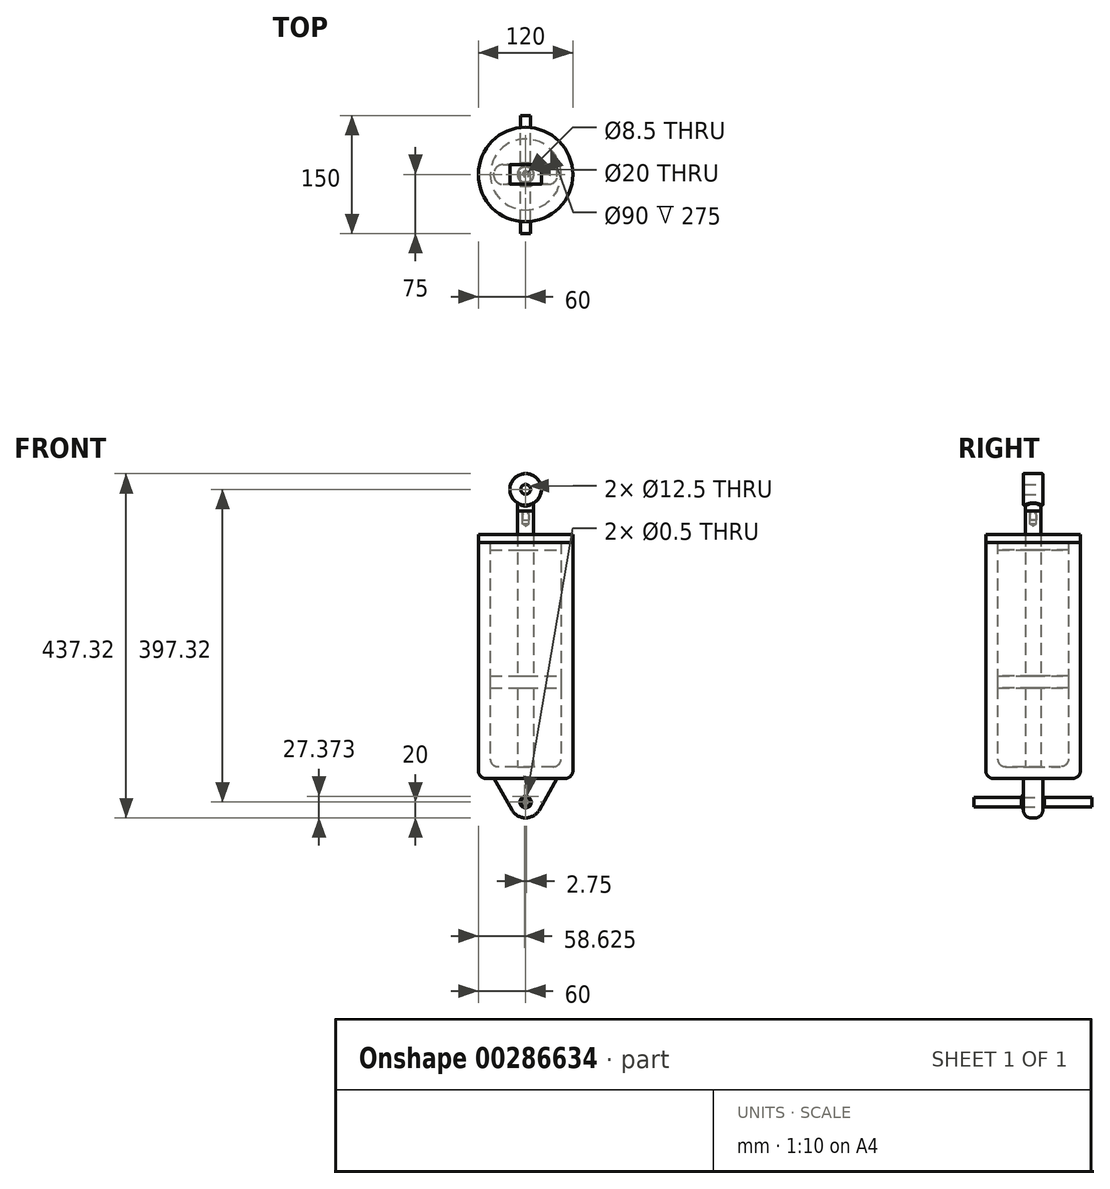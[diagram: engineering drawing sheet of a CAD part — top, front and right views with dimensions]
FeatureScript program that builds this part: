
annotation { "Feature Type Name" : "Feature", "Feature Type Description" : "" }
export const myFeature = defineFeature(function(context is Context, id is Id, definition is map)
    precondition{}
    {
        {
            var Q0;
            Q0=qCreatedBy(makeId("Top.planeOp"),FACE);
            var sketch = newSketch(context, id + "F0", { "sketchPlane" : qUnion([Q0])});
            skCircle(sketch, "E0", {"center": v(0, 0) * mm, "radius": 60 * mm});
            skSolve(sketch);
        }
        {
            var Q0;
            Q0 = qSketchRegion(id + "F0", true);
            extrude(context, id + "F1", {"entities" : qUnion([Q0]), "depth" : 300 * mm});
        }
        {
            var Q0;
            Q0=makeQuery(id+"F1.opExtrude","CAP_FACE",FACE,{"disambiguationData":[OSD([sQuery(id+"F0.wireOp",EDGE,"E0")])],"isStart":false});
            shell(context, id + "F2", {"entities" : qUnion([Q0]), "thickness" : 15 * mm});
        }
        {
            var Q0;
            Q0=qCreatedBy(makeId("Front.planeOp"),FACE);
            var sketch = newSketch(context, id + "F3", { "sketchPlane" : qUnion([Q0])});
            skLineSegment(sketch, "E1", {"start": v(40, 0) * mm, "end": v(17.4, -39.86) * mm});
            skLineSegment(sketch, "E2", {"start": v(-17.4, -39.86) * mm, "end": v(-40, 0) * mm});
            skLineSegment(sketch, "E3", {"start": v(-40, 0) * mm, "end": v(40, 0) * mm});
            skPoint(sketch, "E4.visualSharp", {"position": v(0, -70.55) * mm});
            skArc(sketch, "E4.filletArc", {"start": v(-17.4, -39.86) * mm, "mid": v(0, -50) * mm, "end": v(17.4, -39.86) * mm});
            skLineSegment(sketch, "E5", {"start": v(0, 0) * mm, "end": v(0, -40.4) * mm, "construction": true});
            skCircle(sketch, "E6", {"center": v(0, -30) * mm, "radius": 6.25 * mm});
            skSolve(sketch);
        }
        {
            var Q0;
            Q0 = qSketchRegion(id + "F3", true);
            extrude(context, id + "F4", {"entities" : qUnion([Q0]), "operationType" : NewBodyOperationType.ADD, "endBound" : BoundingType.SYMMETRIC, "depth" : 25 * mm});
        }
        {
            var Q0;
            Q0=makeQuery(id+"F1.opExtrude","CAP_EDGE",EDGE,{"disambiguationData":[OSD([sQuery(id+"F0.wireOp",EDGE,"E0")])],"isStart":true});
            var Q1;
            Q1=makeQuery(id+"F4.opExtrude","CAP_EDGE",EDGE,{"disambiguationData":[OSD([sQuery(id+"F3.wireOp",EDGE,"E3")])],"isStart":true});
            var Q2;
            Q2=makeQuery(id+"F4.opExtrude","CAP_EDGE",EDGE,{"disambiguationData":[OSD([sQuery(id+"F3.wireOp",EDGE,"E3")])],"isStart":false});
            var Q3;
            Q3=makeQuery(id+"F4.opExtrude","CAP_EDGE",EDGE,{"disambiguationData":[OSD([sQuery(id+"F3.wireOp",EDGE,"E2")])],"isStart":false});
            var Q4;
            Q4=makeQuery(id+"F4.opExtrude","CAP_EDGE",EDGE,{"disambiguationData":[OSD([sQuery(id+"F3.wireOp",EDGE,"E2")])],"isStart":true});
            fillet(context, id + "F5", {"entities" : qUnion([Q0, Q1, Q2, Q3, Q4]), "radius" : 10 * mm, "tangentPropagation" : true, "allowEdgeOverflow" : false});
        }
        {
            var Q0;
            {var subQ0=sQuery(id+"F0.wireOp",EDGE,"E0");Q0=makeQuery(id+"F2.opShell","OFFSET_EDGE",EDGE,{"disambiguationData":[OSD([subQ0]),TDD([makeQuery(id+"F1.opExtrude","CAP_EDGE",EDGE,{"disambiguationData":[OSD([subQ0])],"isStart":true})])]});}
            fillet(context, id + "F6", {"entities" : qUnion([Q0]), "radius" : 10 * mm, "tangentPropagation" : true, "allowEdgeOverflow" : false});
        }
        {
            var Q0;
            Q0=qCreatedBy(makeId("Front.planeOp"),FACE);
            var sketch = newSketch(context, id + "F7", { "sketchPlane" : qUnion([Q0])});
            skLineSegment(sketch, "E7", {"start": v(45, 300) * mm, "end": v(45, 290) * mm});
            skLineSegment(sketch, "E8", {"start": v(0, 310) * mm, "end": v(60, 310) * mm});
            skLineSegment(sketch, "E9", {"start": v(60, 310) * mm, "end": v(60, 300) * mm});
            skLineSegment(sketch, "E10", {"start": v(0, 290) * mm, "end": v(45, 290) * mm});
            skLineSegment(sketch, "E11.trimOffspring", {"start": v(45, 300) * mm, "end": v(60, 300) * mm});
            skLineSegment(sketch, "E12", {"start": v(0, 290) * mm, "end": v(0, 310) * mm});
            skPoint(sketch, "E13.end.orphan", {"position": v(-60, 310) * mm});
            skPoint(sketch, "E14.0.start.orphan", {"position": v(-60, 300) * mm});
            skLineSegment(sketch, "E15", {"start": v(0, 0) * mm, "end": v(0, 290) * mm, "construction": true});
            skSolve(sketch);
        }
        {
            var Q0;
            Q0 = qSketchRegion(id + "F7", true);
            var Q1;
            Q1=sQuery(id+"F7.wireOp",EDGE,"E12");
            revolve(context, id + "F8", {"entities" : qUnion([Q0]), "axis" : qUnion([Q1]), "revolveType" : RevolveType.FULL});
        }
        {
            var Q0;
            Q0=qCreatedBy(makeId("Front.planeOp"),FACE);
            var sketch = newSketch(context, id + "F9", { "sketchPlane" : qUnion([Q0])});
            skLineSegment(sketch, "E16", {"start": v(0, 15) * mm, "end": v(0, 340) * mm});
            skLineSegment(sketch, "E17", {"start": v(0, 340) * mm, "end": v(10, 340) * mm});
            skLineSegment(sketch, "E18", {"start": v(10, 340) * mm, "end": v(10, 130) * mm});
            skLineSegment(sketch, "E19", {"start": v(10, 130) * mm, "end": v(45, 130) * mm});
            skLineSegment(sketch, "E20", {"start": v(45, 115) * mm, "end": v(10, 115) * mm});
            skLineSegment(sketch, "E21", {"start": v(10, 115) * mm, "end": v(10, 15) * mm});
            skLineSegment(sketch, "E22", {"start": v(10, 15) * mm, "end": v(0, 15) * mm});
            skLineSegment(sketch, "E23", {"start": v(45, 130) * mm, "end": v(45, 115) * mm});
            skSolve(sketch);
        }
        {
            var Q0;
            Q0 = qSketchRegion(id + "F9", true);
            var Q1;
            Q1=sQuery(id+"F9.wireOp",EDGE,"E16");
            revolve(context, id + "F10", {"entities" : qUnion([Q0]), "axis" : qUnion([Q1]), "revolveType" : RevolveType.FULL});
        }
        {
            var Q0;
            Q0=makeQuery(id+"F10.opRevolve","SWEPT_BODY",BODY,{"disambiguationData":[OSD([sQuery(id+"F9.wireOp",EDGE,"E16"),sQuery(id+"F9.wireOp",EDGE,"E17"),sQuery(id+"F9.wireOp",EDGE,"E18"),sQuery(id+"F9.wireOp",EDGE,"E19"),sQuery(id+"F9.wireOp",EDGE,"E20"),sQuery(id+"F9.wireOp",EDGE,"E21"),sQuery(id+"F9.wireOp",EDGE,"E22"),sQuery(id+"F9.wireOp",EDGE,"E23")])]});
            var Q1;
            Q1=makeQuery(id+"F8.opRevolve","SWEPT_BODY",BODY,{"disambiguationData":[OSD([sQuery(id+"F7.wireOp",EDGE,"E7"),sQuery(id+"F7.wireOp",EDGE,"E8"),sQuery(id+"F7.wireOp",EDGE,"E9"),sQuery(id+"F7.wireOp",EDGE,"E10"),sQuery(id+"F7.wireOp",EDGE,"E11.trimOffspring"),sQuery(id+"F7.wireOp",EDGE,"E12")])]});
            booleanBodies(context, id + "F11", {"operationType" : BooleanOperationType.SUBTRACTION, "tools" : qUnion([Q0]), "targets" : qUnion([Q1]), "keepTools" : true});
        }
        {
            var Q0;
            Q0=makeQuery(id+"F10.opRevolve","SWEPT_FACE",FACE,{"disambiguationData":[OSD([sQuery(id+"F9.wireOp",EDGE,"E17")])]});
            var sketch = newSketch(context, id + "F12", { "sketchPlane" : qUnion([Q0])});
            skPoint(sketch, "E24", {"position": v(0, 0) * mm});
            skSolve(sketch);
        }
        {
            var Q0;
            Q0=sQuery(id+"F12.wireOp",VERTEX,"E24");
            var Q1;
            Q1=makeQuery(id+"F10.opRevolve","SWEPT_BODY",BODY,{"disambiguationData":[OSD([sQuery(id+"F9.wireOp",EDGE,"E16"),sQuery(id+"F9.wireOp",EDGE,"E17"),sQuery(id+"F9.wireOp",EDGE,"E18"),sQuery(id+"F9.wireOp",EDGE,"E19"),sQuery(id+"F9.wireOp",EDGE,"E20"),sQuery(id+"F9.wireOp",EDGE,"E21"),sQuery(id+"F9.wireOp",EDGE,"E22"),sQuery(id+"F9.wireOp",EDGE,"E23")])]});
            hole(context, id + "F13", {"style" : HoleStyle.SIMPLE, "endStyle" : HoleEndStyle.BLIND, "standardTappedOrClearance" : lookupTablePath({ "standard" : "ISO", "fit" : "Normal", "engagement" : "75%", "pitch" : "1.5 mm", "size" : "M10", "type" : "Tapped" }), "standardBlindInLast" : lookupTablePath({ "fit" : "Standard", "standard" : "ISO", "engagement" : "75%", "pitch" : "1.5 mm", "size" : "M10", "type" : "Tapped" }), "holeDiameter" : 8.5 * mm, "showTappedDepth" : true, "holeDepth" : 16.5 * mm, "tappedDepth" : 12 * mm, "tapClearance" : 3, "locations" : qUnion([Q0]), "scope" : qUnion([Q1]), "majorDiameter" : 10 * mm});
        }
        {
            var Q0;
            Q0=qCreatedBy(makeId("Front.planeOp"),FACE);
            var sketch = newSketch(context, id + "F14", { "sketchPlane" : qUnion([Q0])});
            skLineSegment(sketch, "E25", {"start": v(4.25, 334) * mm, "end": v(4.25, 328.5) * mm});
            skLineSegment(sketch, "E26", {"start": v(0, 328.5) * mm, "end": v(4.25, 328.5) * mm});
            skLineSegment(sketch, "E27.0", {"start": v(10, 340) * mm, "end": v(5.14, 340) * mm});
            skLineSegment(sketch, "E28", {"start": v(0, 328.5) * mm, "end": v(0, 350) * mm});
            skLineSegment(sketch, "E29", {"start": v(0, 350) * mm, "end": v(10, 350) * mm});
            skLineSegment(sketch, "E30", {"start": v(10, 350) * mm, "end": v(10, 340) * mm});
            skPoint(sketch, "E31.start.orphan", {"position": v(-4.25, 328.5) * mm});
            skPoint(sketch, "E32.orphan", {"position": v(-10, 340) * mm});
            skPoint(sketch, "E33", {"position": v(0, 340) * mm});
            skLineSegment(sketch, "E34", {"start": v(3.14, 338) * mm, "end": v(3.14, 337) * mm});
            skLineSegment(sketch, "E35", {"start": v(3.4, 336) * mm, "end": v(3.98, 335) * mm});
            skPoint(sketch, "E36.visualSharp", {"position": v(3.14, 338.83) * mm});
            skArc(sketch, "E36.filletArc", {"start": v(5.14, 340) * mm, "mid": v(3.72, 339.41) * mm, "end": v(3.14, 338) * mm});
            skPoint(sketch, "E37.visualSharp", {"position": v(4.25, 334.54) * mm});
            skArc(sketch, "E37.filletArc", {"start": v(4.25, 334) * mm, "mid": v(4.18, 334.52) * mm, "end": v(3.98, 335) * mm});
            skPoint(sketch, "E38.visualSharp", {"position": v(3.14, 336.46) * mm});
            skArc(sketch, "E38.filletArc", {"start": v(3.14, 337) * mm, "mid": v(3.2, 336.48) * mm, "end": v(3.4, 336) * mm});
            skSolve(sketch);
        }
        {
            var Q0;
            Q0 = qSketchRegion(id + "F14", true);
            var Q1;
            Q1=sQuery(id+"F14.wireOp",EDGE,"E28");
            revolve(context, id + "F15", {"entities" : qUnion([Q0]), "axis" : qUnion([Q1]), "revolveType" : RevolveType.FULL});
        }
        {
            var Q0;
            Q0=qCreatedBy(makeId("Front.planeOp"),FACE);
            var sketch = newSketch(context, id + "F16", { "sketchPlane" : qUnion([Q0])});
            skCircle(sketch, "E39", {"center": v(0, 367.32) * mm, "radius": 20 * mm});
            skCircle(sketch, "E40", {"center": v(0, 367.32) * mm, "radius": 6.25 * mm});
            skSolve(sketch);
        }
        {
            var Q0;
            Q0 = qSketchRegion(id + "F16", true);
            extrude(context, id + "F17", {"entities" : qUnion([Q0]), "operationType" : NewBodyOperationType.ADD, "endBound" : BoundingType.SYMMETRIC, "depth" : 25 * mm});
        }
        {
            var Q0;
            Q0=makeQuery(id+"F17.opExtrude","CAP_EDGE",EDGE,{"disambiguationData":[OSD([sQuery(id+"F16.wireOp",EDGE,"E39")])],"isStart":false});
            var Q1;
            Q1=makeQuery(id+"F17.opExtrude","CAP_EDGE",EDGE,{"disambiguationData":[OSD([sQuery(id+"F16.wireOp",EDGE,"E39")])],"isStart":true});
            var Q2;
            Q2=makeQuery(id+"F17.boolean.opBoolean","INTERSECT",EDGE,{"derivedFrom":[makeQuery(id+"F15.opRevolve","SWEPT_FACE",FACE,{"disambiguationData":[OSD([sQuery(id+"F14.wireOp",EDGE,"E30")])]}),makeQuery(id+"F17.opExtrude","SWEPT_FACE",FACE,{"disambiguationData":[OSD([sQuery(id+"F16.wireOp",EDGE,"E39")])]})]});
            var Q3;
            Q3=makeQuery(id+"F17.opExtrude","CAP_EDGE",EDGE,{"disambiguationData":[OSD([sQuery(id+"F16.wireOp",EDGE,"E40")])],"isStart":false});
            var Q4;
            Q4=makeQuery(id+"F17.opExtrude","CAP_EDGE",EDGE,{"disambiguationData":[OSD([sQuery(id+"F16.wireOp",EDGE,"E40")])],"isStart":true});
            fillet(context, id + "F18", {"entities" : qUnion([Q0, Q1, Q2, Q3, Q4]), "radius" : 1 * mm, "tangentPropagation" : true, "allowEdgeOverflow" : false});
        }
        {
            var Q0;
            Q0=qCreatedBy(makeId("Right.planeOp"),FACE);
            var sketch = newSketch(context, id + "F19", { "sketchPlane" : qUnion([Q0])});
            skLineSegment(sketch, "E41", {"start": v(12.5, -36.25) * mm, "end": v(-12.5, -36.25) * mm});
            skLineSegment(sketch, "E42", {"start": v(-12.5, -23.75) * mm, "end": v(12.5, -23.75) * mm, "construction": true});
            skLineSegment(sketch, "E43", {"start": v(12.5, -30) * mm, "end": v(-12.5, -30) * mm, "construction": true});
            skLineSegment(sketch, "E44", {"start": v(12.5, -36.25) * mm, "end": v(12.5, -34.25) * mm});
            skLineSegment(sketch, "E45", {"start": v(12.5, -34.25) * mm, "end": v(14.5, -34.25) * mm});
            skLineSegment(sketch, "E46", {"start": v(14.5, -34.25) * mm, "end": v(14.5, -36.25) * mm});
            skLineSegment(sketch, "E47", {"start": v(14.5, -36.25) * mm, "end": v(75, -36.25) * mm});
            skLineSegment(sketch, "E48", {"start": v(75, -36.25) * mm, "end": v(75, -30) * mm});
            skLineSegment(sketch, "E49", {"start": v(75, -30) * mm, "end": v(-75, -30) * mm});
            skLineSegment(sketch, "E50", {"start": v(-75, -30) * mm, "end": v(-75, -36.25) * mm});
            skLineSegment(sketch, "E51", {"start": v(-75, -36.25) * mm, "end": v(-14.5, -36.25) * mm});
            skLineSegment(sketch, "E52", {"start": v(-14.5, -36.25) * mm, "end": v(-14.5, -34.25) * mm});
            skLineSegment(sketch, "E53", {"start": v(-14.5, -34.25) * mm, "end": v(-12.5, -34.25) * mm});
            skLineSegment(sketch, "E54", {"start": v(-12.5, -34.25) * mm, "end": v(-12.5, -36.25) * mm});
            skLineSegment(sketch, "E55", {"start": v(0, 0) * mm, "end": v(0, -56.18) * mm, "construction": true});
            skSolve(sketch);
        }
        {
            var Q0;
            Q0 = qSketchRegion(id + "F19", true);
            var Q1;
            Q1=sQuery(id+"F19.wireOp",EDGE,"E49");
            revolve(context, id + "F20", {"entities" : qUnion([Q0]), "axis" : qUnion([Q1]), "revolveType" : RevolveType.FULL});
        }
        {
            var Q0;
            Q0=makeQuery(id+"F4.opExtrude","CAP_FACE",FACE,{"disambiguationData":[OSD([sQuery(id+"F3.wireOp",EDGE,"E1"),sQuery(id+"F3.wireOp",EDGE,"E2"),sQuery(id+"F3.wireOp",EDGE,"E3"),sQuery(id+"F3.wireOp",EDGE,"E4.filletArc"),sQuery(id+"F3.wireOp",EDGE,"E6")])],"isStart":false});
            var sketch = newSketch(context, id + "F21", { "sketchPlane" : qUnion([Q0])});
            skArc(sketch, "E56", {"start": v(-2.34, -23.14) * mm, "mid": v(0, -37.25) * mm, "end": v(2.34, -23.14) * mm});
            skLineSegment(sketch, "E57", {"start": v(-60, 10) * mm, "end": v(-60, 300) * mm});
            skLineSegment(sketch, "E58", {"start": v(60, 300) * mm, "end": v(60, 10) * mm});
            skArc(sketch, "E59.0", {"start": v(-1.42, -26) * mm, "mid": v(0, -34.25) * mm, "end": v(1.42, -26) * mm});
            skLineSegment(sketch, "E60", {"start": v(-0.75, -25.05) * mm, "end": v(-0.75, -22.79) * mm});
            skLineSegment(sketch, "E61", {"start": v(0.75, -25.05) * mm, "end": v(0.75, -22.79) * mm});
            skLineSegment(sketch, "E62", {"start": v(-0.75, -22.79) * mm, "end": v(-0.75, -22.2) * mm});
            skLineSegment(sketch, "E63", {"start": v(-0.95, -22) * mm, "end": v(-1.8, -22) * mm});
            skLineSegment(sketch, "E64", {"start": v(-2, -22.2) * mm, "end": v(-2, -22.66) * mm});
            skLineSegment(sketch, "E65", {"start": v(0.75, -22.79) * mm, "end": v(0.75, -22.2) * mm});
            skLineSegment(sketch, "E66", {"start": v(0.95, -22) * mm, "end": v(1.8, -22) * mm});
            skLineSegment(sketch, "E67", {"start": v(2, -22.2) * mm, "end": v(2, -22.66) * mm});
            skPoint(sketch, "E68.visualSharp", {"position": v(-0.75, -25.82) * mm});
            skArc(sketch, "E68.filletArc", {"start": v(-1.42, -26) * mm, "mid": v(-0.93, -25.63) * mm, "end": v(-0.75, -25.05) * mm});
            skPoint(sketch, "E69.visualSharp", {"position": v(0.75, -25.82) * mm});
            skArc(sketch, "E69.filletArc", {"start": v(0.75, -25.05) * mm, "mid": v(0.93, -25.63) * mm, "end": v(1.42, -26) * mm});
            skPoint(sketch, "E70.visualSharp", {"position": v(-2, -23.03) * mm});
            skArc(sketch, "E70.filletArc", {"start": v(-2.34, -23.14) * mm, "mid": v(-2.1, -22.96) * mm, "end": v(-2, -22.66) * mm});
            skPoint(sketch, "E71.visualSharp", {"position": v(2, -23.03) * mm});
            skArc(sketch, "E71.filletArc", {"start": v(2, -22.66) * mm, "mid": v(2.1, -22.96) * mm, "end": v(2.34, -23.14) * mm});
            skPoint(sketch, "E72.visualSharp", {"position": v(2, -22) * mm});
            skArc(sketch, "E72.filletArc", {"start": v(2, -22.2) * mm, "mid": v(1.94, -22.06) * mm, "end": v(1.8, -22) * mm});
            skPoint(sketch, "E73.visualSharp", {"position": v(0.75, -22) * mm});
            skArc(sketch, "E73.filletArc", {"start": v(0.95, -22) * mm, "mid": v(0.8, -22.06) * mm, "end": v(0.75, -22.2) * mm});
            skPoint(sketch, "E74.visualSharp", {"position": v(-0.75, -22) * mm});
            skArc(sketch, "E74.filletArc", {"start": v(-0.75, -22.2) * mm, "mid": v(-0.8, -22.06) * mm, "end": v(-0.95, -22) * mm});
            skPoint(sketch, "E75.visualSharp", {"position": v(-2, -22) * mm});
            skArc(sketch, "E75.filletArc", {"start": v(-1.8, -22) * mm, "mid": v(-1.94, -22.06) * mm, "end": v(-2, -22.2) * mm});
            skCircle(sketch, "E76", {"center": v(-1.38, -22.63) * mm, "radius": 0.25 * mm});
            skCircle(sketch, "E77", {"center": v(1.38, -22.63) * mm, "radius": 0.25 * mm});
            skLineSegment(sketch, "E78", {"start": v(-1.38, -22.63) * mm, "end": v(-1.38, -22) * mm, "construction": true});
            skLineSegment(sketch, "E79", {"start": v(1.38, -22.63) * mm, "end": v(1.38, -22) * mm, "construction": true});
            skSolve(sketch);
        }
        {
            var Q0;
            Q0 = qSketchRegion(id + "F21", true);
            var Q1;
            Q1=makeQuery(id+"F20.opRevolve","SWEPT_FACE",FACE,{"disambiguationData":[OSD([sQuery(id+"F19.wireOp",EDGE,"E52")])]});
            extrude(context, id + "F22", {"entities" : qUnion([Q0]), "endBound" : BoundingType.UP_TO_SURFACE, "endBoundEntityFace" : qUnion([Q1]), "depth" : 25 * mm});
        }
        {
            var Q0;
            Q0=makeQuery(id+"F22.opExtrude","CAP_EDGE",EDGE,{"disambiguationData":[OSD([sQuery(id+"F21.wireOp",EDGE,"E59.0")])],"isStart":false});
            var Q1;
            Q1=makeQuery(id+"F22.opExtrude","CAP_EDGE",EDGE,{"disambiguationData":[OSD([sQuery(id+"F21.wireOp",EDGE,"E56")])],"isStart":true});
            fillet(context, id + "F23", {"entities" : qUnion([Q0, Q1]), "radius" : 0.2 * mm, "tangentPropagation" : true, "allowEdgeOverflow" : false});
        }
    });
